# Revit family: Gewindeplatte 2-Loch M10
name_source: partatom
category: HLS-Bauteile
revit_build: Autodesk Revit 2017 (Build: 20190507_1515(x64)
units: mm (PartAtom-declared; Revit-internal decimal feet)

## family parameters
Arbeitsebenenbasiert = Ja
Beim Laden mit Abzugskörper schneiden = Nein
Bemaßung runder Anschluss = Durchmesser verwenden
Gemeinsam genutzt = Ja
Immer vertikal = Nein
Raumberechnungspunkt = Nein
Teiletyp = Normal

## types (1)
- Gewindeplatte 2-Loch M10
    Artikelnummer = 0816092
    B = 30 mm  [stored 0.0984252 ft]
    Breite = 30 mm  [stored 0.0984252 ft]
    EAN = 4250928420152
    Fabrikat = MEFA
    Firma = MEFA Befestigungs- und Montagesysteme GmbH
    Gewicht = 0.07 kg
    Gewicht pro Bauteil = 0.07 kg
    Kurztext1 = Gewindeplatte 2-Loch
    Kurztext2 = M10 vierkant 65 x 30 mm gvz
    L = 65 mm  [stored 0.213255 ft]
    Länge = 65 mm  [stored 0.213255 ft]
    Material = Stahl
    Materialname = S235
    Mengeneinheit = St
    Oberflaeche = galvanisch verzinkt
    Profiltyp = 35, Stex 35
    S = 5 mm  [stored 0.0164042 ft]
    Stärke = 0 mm  [stored 0 ft]
    Vorgabe-Ansicht = 1219 mm
    vpe = 50 St

note: [stored X ft] marks values corroborated as IEEE doubles in the binary element streams (Revit-internal decimal feet)
